# Revit family: HUNTER_A2C-Decoder Wall Mounted
name_source: partatom
category: Electrical Equipment
revit_build: Autodesk Revit 2017 (Build: 20160225_1515(x64)
units: mm (PartAtom-declared; Revit-internal decimal feet)

## family parameters
Cut with Voids When Loaded = No
Host = Face
OmniClass Number = 23.35.25.21
Panel Configuration = One Column
Part Type = Panelboard
Room Calculation Point = No
Round Connector Dimension = Use Diameter
Shared = Yes

## types (3) — shared parameters
Assembly Code = D5090900
Current = 2 A
Decoders = Hunter ICD Decoders / Expandable Up to 225 stations
Default Elevation = 1200 mm
Enclosure_Depth = 170 mm  [stored 0.557743 ft]
Enclosure_Height = 393 mm
Enclosure_Width = 393 mm
Expansion Module = A2C-D75 (75 Stations plug-in) Expansion Module
Input Voltage = 120 V
Keynote = 328423.04
Manufacturer = Hunter® Industries
Number of Sensor Inputs = Flow Input and sensor decoder
Output Voltage = 24 V
Panel Type = Modular Decoder
Power = 240 VA
Power factor = 1
Sensor Input = 3 Clik, 1 Solar Sync, and 6 Flow sensor
Stations = 75-225 Decoder Stations
Transformer Output = 24VAC, 4.0A
Type Comments = Hunter's Flagship Controller
Type Image = <None>
URL = https://www.hunterindustries.com
Voltage = 120

## per-type parameters (varying)
| type | Description | Enclosure Material | Model | Protection Rating |
| A2C-75D-M | 75-station base model expandable , Metal wall mount enclosure | Hunter® Metal Grey | ACC-75D-M Expandable Up to 225 stations with Decoders | IP44 |
| A2C-75D-SS | 75-station base model expandable , Stainless steel wall mount enclosure | Hunter® Stainless Steel | ACC-75D-SS Expandable Up to 225 stations with Decoders | IP44 |
| A2C-75D-P | 75-station base model expandable , Plastic wall mount enclosure | Hunter® Plastic | ACC-75D-P Expandable Up to 225 stations with Decoders | IP24 |

note: [stored X ft] marks values corroborated as IEEE doubles in the binary element streams (Revit-internal decimal feet)

## geometry (parser evidence)
native form markers: Sweep x4
no freeform markers — native parametric forms only
